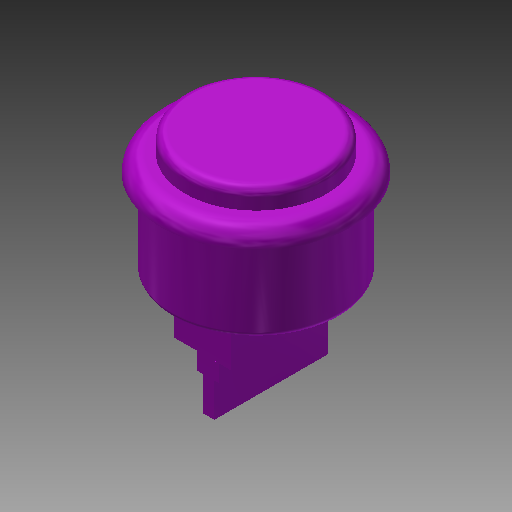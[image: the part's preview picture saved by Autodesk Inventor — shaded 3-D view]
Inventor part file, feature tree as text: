
AUTODESK INVENTOR PART (.ipt)
format: ipt  version: 2019 (Build 230136000, 136)  size: 216,576 bytes
history: native  units: mm
features: extrude x6, sketch x6, fillet x3
ambient origin geometry x8: Origin, YZ Plane, XZ Plane, XY Plane, X Axis, Y Axis, Z Axis, Center Point
bodies: Solid1 (feature_tree)
feature tree (15):
  extrude  "Extrusion1"  Depth=33.5mm
  extrude  "Extrusion2"  Depth=6.5mm TaperAngle=0.0deg
  fillet  "Fillet1"  Radius=1.5mm
  fillet  "Fillet2"  Radius=2.95mm
  extrude  "Extrusion5"  Depth=15.0mm TaperAngle=0.0deg
  extrude  "Extrusion7"  Depth=20.0mm
  extrude  "Extrusion8"  Depth=4.0mm
  extrude  "Extrusion10"  Depth=3.0mm TaperAngle=0.0deg
  fillet  "Fillet3"  Radius=6.0mm
  sketch  "Sketch1"  dims[d0=25.0mm d1=33.5mm]
  sketch  "Sketch2"  dims[d4=3.0mm d5=0.0mm d6=25.0mm d10=6.5mm d11=0.0mm d18=1.5mm d19=2.95mm]
  sketch  "Sketch5"  dims[d23=29.5mm d24=15.0mm d25=0.0mm]
  sketch  "Sketch7"  dims[d30=10.0mm d32=20.0mm]
  sketch  "Sketch8"  dims[d33=8.0mm d34=0.0mm d35=4.0mm]
  sketch  "Sketch10"  dims[d37=20.0mm d38=3.0mm d39=0.0mm d44=6.0mm d45=0.0mm d46=20.0mm d48=2.0mm d49=1.0mm]
